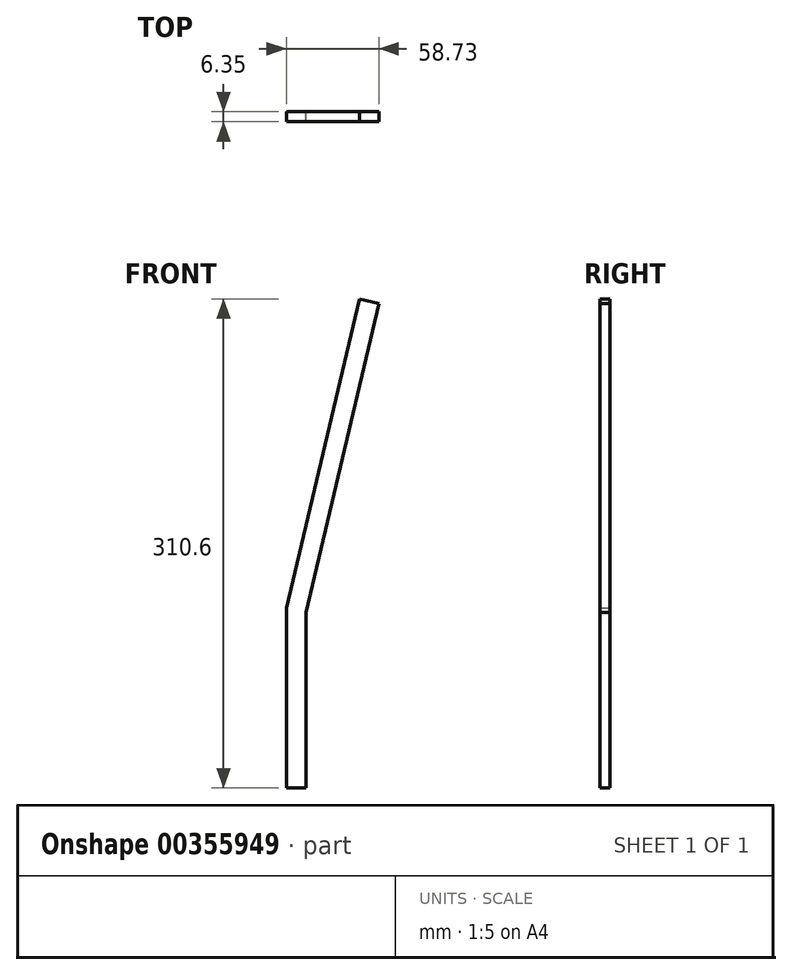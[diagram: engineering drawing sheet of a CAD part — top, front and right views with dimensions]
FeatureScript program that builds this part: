
annotation { "Feature Type Name" : "Feature", "Feature Type Description" : "" }
export const myFeature = defineFeature(function(context is Context, id is Id, definition is map)
    precondition{}
    {
        {
            var Q0;
            Q0=qCreatedBy(makeId("Front.planeOp"),FACE);
            var sketch = newSketch(context, id + "F0", { "sketchPlane" : qUnion([Q0])});
            skLineSegment(sketch, "E0", {"start": v(0, 0) * mm, "end": v(46.72, 197.76) * mm, "construction": true});
            skLineSegment(sketch, "E1", {"start": v(46.72, 197.76) * mm, "end": v(40.54, 199.22) * mm});
            skLineSegment(sketch, "E2", {"start": v(0, 0) * mm, "end": v(-12.36, 2.92) * mm});
            skLineSegment(sketch, "E3", {"start": v(0, 0) * mm, "end": v(12.36, -2.92) * mm});
            skLineSegment(sketch, "E4", {"start": v(46.72, 197.76) * mm, "end": v(52.9, 196.3) * mm});
            skLineSegment(sketch, "E5", {"start": v(-12.36, -111.38) * mm, "end": v(12.36, -111.38) * mm});
            skPoint(sketch, "E6.trimOffspring.end.orphan", {"position": v(12.36, -35.18) * mm});
            skPoint(sketch, "E7.end.orphan", {"position": v(-12.36, -35.18) * mm});
            skLineSegment(sketch, "E8", {"start": v(40.54, 199.22) * mm, "end": v(-5.83, 2.92) * mm});
            skLineSegment(sketch, "E9", {"start": v(52.9, 196.3) * mm, "end": v(6.52, 0) * mm});
            skLineSegment(sketch, "E10", {"start": v(6.52, 0) * mm, "end": v(6.52, -111.38) * mm});
            skLineSegment(sketch, "E11", {"start": v(-5.83, 2.92) * mm, "end": v(-5.83, -111.38) * mm});
            skPoint(sketch, "E12.center.orphan", {"position": v(0, -35.18) * mm});
            skSolve(sketch);
        }
        {
            var Q0;
            Q0=qSketchRegion(id+"F0",true);
            extrude(context, id + "F1", {"entities" : qUnion([Q0]), "depth" : 6.35 * mm});
        }
    });
